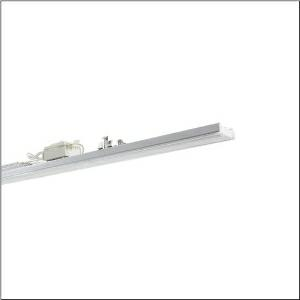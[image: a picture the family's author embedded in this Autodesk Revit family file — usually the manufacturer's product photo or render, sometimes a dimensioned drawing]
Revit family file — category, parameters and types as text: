
# Revit family: licross_r__21_recessed_ho_52tl12dn4fxm3c_2914
name_source: partatom
category: Lighting Fixtures
units: mm (PartAtom-declared; Revit-internal decimal feet)

## family parameters
Cut with Voids When Loaded = No
Host = Face
Light Source = No
Part Type = Normal
Room Calculation Point = No
Round Connector Dimension = Use Diameter
Shared = No

## types (1)
- --- (1 x LED, 930 lm, 7.5 W, 4000K)
    Apparent Load = 8 VA
    CIE Flux Codes = 69 91 98 100 100
    Color Rendering = 80
    Color Temperature = 4000K
    Default Elevation = 1800 mm
    Description = Licross® 21 Recessed HO, luminaire insert, of sheet steel, galvanised, coil coated, white, length: 1.500mm, width: 66mm, height: 67mm, LED rated luminous flux: 15.000lm, light colour: 840, control gear: DALI 2 (for two DALI lines), with plug, 6-pole, with phase selection, for trunking rail, 14-core, mains connection: 220..240V, AC, 50/60Hz, rated input power: 88W, halogen-free wiring, for emergency light function, for trunking rail, 14-core, converter,control gear: single battery element, battery: LiFePO4, 9Ah, primary optical cover: cover, of PMMA, light emission: direct distribution, primary light characteristic: symmetric, protection rating (complete): IP40, insulation class (complete): insulation class I (protective earthing), certification: CE, UKCA, protection symbol: D if used in an environment without relevant dust loads with corresponding accessories, impact resistance: IK06, permissible ambient temperature for indoor applications: +5..+30°C, standard: EN 60598-2-22, LABS conformity tested according to VDMA 24364:2018-05, reducing of maximum allowable ambient temperature of 5°C with ceiling mounting, corresponds to IFS (International Featured Standards) requirements for safety and quality in the food industry, packaging unit: 1 piece
    Height = 58 mm
    Lamp = 1 x LED
    Lamp Light Flux = 930 lm
    Lamp Power = 7.5 W
    Lamp count = 1
    Length = 1500 mm
    Luminous efficacy = 124 lm/W
    Manufacturer = Siteco
    ModVariant = No
    Model = 52TL12DN4FXM3C
    Mounting Place = Ceiling
    Mounting Type = Pendant
    Number of Poles = 1
    OnlyDefault = Yes
    Power Factor = 1
    Product Name = Licross® 21 Recessed HO
    Product group = luminaire insert
    ProductGroupID = 902
    Protection Class = Protection class I
    Protection Degree = IP 40
    RLX_Detail_Level = 1
    RLX_Emergency_Light_Flux = 0 lm
    RLX_Emergency_Type = 0
    RLX_Emergency_Type_DB = No
    RlxData = <blob elided: 25129 chars, md5=f3826bc4>
    Socket = socket
    Standby Power = 0 W
    System Light Flux = 930 lm
    System Power = 8 W
    Type Comments = : emergency light operation: 3 h
    Type Image = l_1296930.jpg
    URL = http://relux.com
    VarID = @adj_109320
    Voltage = 0 V
    Weight = 0.00 kg
    Width = 66 mm

## geometry (parser evidence)
native form markers: Blend x4, Sweep x13
no freeform markers — native parametric forms only
